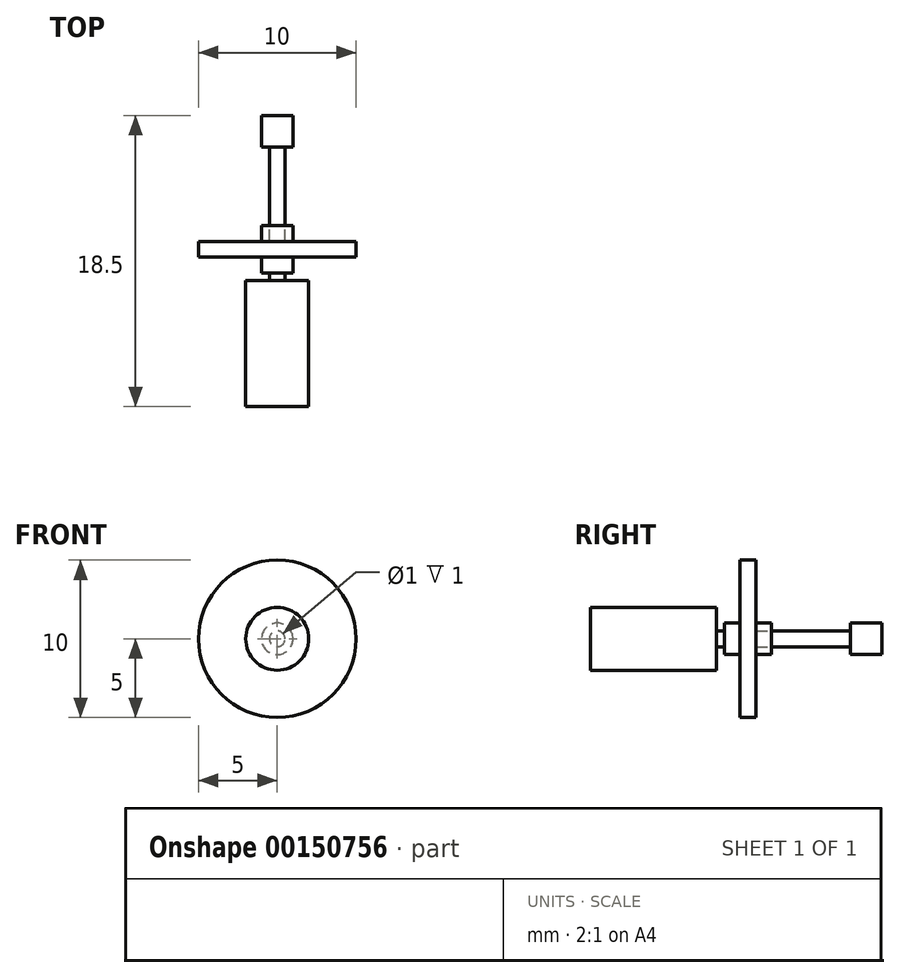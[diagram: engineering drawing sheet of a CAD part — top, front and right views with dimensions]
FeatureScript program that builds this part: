
annotation { "Feature Type Name" : "Feature", "Feature Type Description" : "" }
export const myFeature = defineFeature(function(context is Context, id is Id, definition is map)
    precondition{}
    {
        {
            var Q0;
            Q0=qCreatedBy(makeId("Front.planeOp"),FACE);
            var sketch = newSketch(context, id + "F0", { "sketchPlane" : qUnion([Q0])});
            skCircle(sketch, "E0", {"center": v(0, 0) * mm, "radius": 1 * mm});
            skSolve(sketch);
        }
        {
            var Q0;
            Q0=makeQuery(id+"F0.imprint","IMPRINT",FACE,{"disambiguationData":[TD([[makeQuery(id+"F0.imprint","IMPRINT",EDGE,{"derivedFrom":sQuery(id+"F0.wireOp",EDGE,"E0")}),1.0]])]});
            extrude(context, id + "F1", {"entities" : qUnion([Q0]), "depth" : 2 * mm});
        }
        {
            var Q0;
            Q0=makeQuery(id+"F1.opExtrude","CAP_FACE",FACE,{"disambiguationData":[OSD([sQuery(id+"F0.wireOp",EDGE,"E0")])],"isStart":false});
            var sketch = newSketch(context, id + "F2", { "sketchPlane" : qUnion([Q0])});
            skCircle(sketch, "E1", {"center": v(0, 0) * mm, "radius": 0.5 * mm});
            skSolve(sketch);
        }
        {
            var Q0;
            Q0=makeQuery(id+"F2.imprint","IMPRINT",FACE,{"disambiguationData":[TD([[makeQuery(id+"F2.imprint","IMPRINT",EDGE,{"derivedFrom":sQuery(id+"F2.wireOp",EDGE,"E1")}),1.0]])]});
            extrude(context, id + "F3", {"entities" : qUnion([Q0]), "operationType" : NewBodyOperationType.ADD, "depth" : 5 * mm});
        }
        {
            var Q0;
            Q0=makeQuery(id+"F3.opExtrude","CAP_FACE",FACE,{"disambiguationData":[OSD([sQuery(id+"F2.wireOp",EDGE,"E1")])],"isStart":false});
            var sketch = newSketch(context, id + "F4", { "sketchPlane" : qUnion([Q0])});
            skCircle(sketch, "E2", {"center": v(0, 0) * mm, "radius": 1 * mm});
            skSolve(sketch);
        }
        {
            var Q0;
            Q0=makeQuery(id+"F4.imprint","IMPRINT",FACE,{"disambiguationData":[TD([[makeQuery(id+"F4.imprint","IMPRINT",EDGE,{"derivedFrom":sQuery(id+"F4.wireOp",EDGE,"E2")}),1.0]])]});
            extrude(context, id + "F5", {"entities" : qUnion([Q0]), "depth" : 1 * mm});
        }
        {
            var Q0;
            Q0=makeQuery(id+"F5.opExtrude","CAP_FACE",FACE,{"disambiguationData":[OSD([sQuery(id+"F2.wireOp",EDGE,"E1"),sQuery(id+"F4.wireOp",EDGE,"E2")])],"isStart":false});
            var sketch = newSketch(context, id + "F6", { "sketchPlane" : qUnion([Q0])});
            skCircle(sketch, "E3", {"center": v(0, 0) * mm, "radius": 5 * mm});
            skSolve(sketch);
        }
        {
            var Q0;
            Q0 = qSketchRegion(id + "F6", true);
            extrude(context, id + "F7", {"entities" : qUnion([Q0]), "operationType" : NewBodyOperationType.ADD, "depth" : 1 * mm});
        }
        {
            var Q0;
            Q0=makeQuery(id+"F7.opExtrude","CAP_FACE",FACE,{"disambiguationData":[OSD([sQuery(id+"F6.wireOp",EDGE,"E3")])],"isStart":false});
            var sketch = newSketch(context, id + "F8", { "sketchPlane" : qUnion([Q0])});
            skCircle(sketch, "E4", {"center": v(0, 0) * mm, "radius": 1 * mm});
            skSolve(sketch);
        }
        {
            var Q0;
            Q0=makeQuery(id+"F8.imprint","IMPRINT",FACE,{"disambiguationData":[TD([[makeQuery(id+"F8.imprint","IMPRINT",EDGE,{"derivedFrom":sQuery(id+"F8.wireOp",EDGE,"E4")}),1.0]])]});
            extrude(context, id + "F9", {"entities" : qUnion([Q0]), "operationType" : NewBodyOperationType.ADD, "depth" : 1 * mm});
        }
        {
            var Q0;
            Q0=makeQuery(id+"F9.opExtrude","CAP_FACE",FACE,{"disambiguationData":[OSD([sQuery(id+"F8.wireOp",EDGE,"E4")])],"isStart":false});
            var sketch = newSketch(context, id + "F10", { "sketchPlane" : qUnion([Q0])});
            skCircle(sketch, "E5", {"center": v(0, 0) * mm, "radius": 0.5 * mm});
            skSolve(sketch);
        }
        {
            var Q0;
            Q0=makeQuery(id+"F10.imprint","IMPRINT",FACE,{"disambiguationData":[TD([[makeQuery(id+"F10.imprint","IMPRINT",EDGE,{"derivedFrom":sQuery(id+"F10.wireOp",EDGE,"E5")}),1.0]])]});
            extrude(context, id + "F11", {"entities" : qUnion([Q0]), "operationType" : NewBodyOperationType.ADD, "depth" : 0.5 * mm});
        }
        {
            var Q0;
            Q0=makeQuery(id+"F11.opExtrude","CAP_FACE",FACE,{"disambiguationData":[OSD([sQuery(id+"F10.wireOp",EDGE,"E5")])],"isStart":false});
            var sketch = newSketch(context, id + "F12", { "sketchPlane" : qUnion([Q0])});
            skCircle(sketch, "E6", {"center": v(0, 0) * mm, "radius": 2 * mm});
            skSolve(sketch);
        }
        {
            var Q0;
            Q0 = qSketchRegion(id + "F12", true);
            extrude(context, id + "F13", {"entities" : qUnion([Q0]), "operationType" : NewBodyOperationType.ADD, "depth" : 8 * mm});
        }
    });
